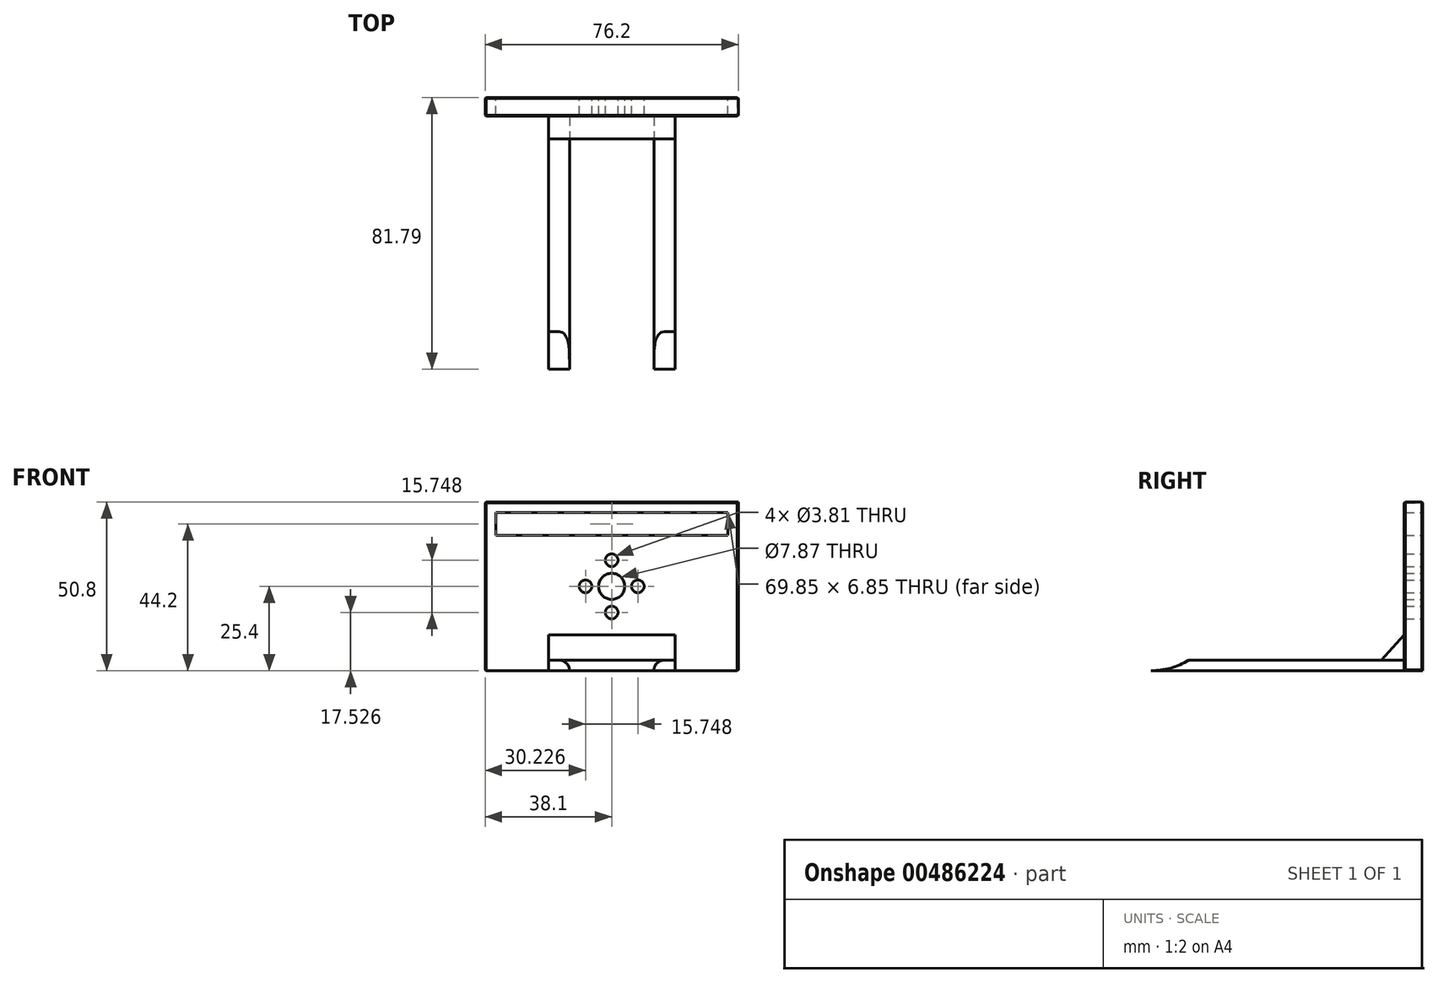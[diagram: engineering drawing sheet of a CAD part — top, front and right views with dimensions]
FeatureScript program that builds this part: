
annotation { "Feature Type Name" : "Feature", "Feature Type Description" : "" }
export const myFeature = defineFeature(function(context is Context, id is Id, definition is map)
    precondition{}
    {
        {
            var Q0;
            Q0=qCreatedBy(makeId("Front.planeOp"),FACE);
            var sketch = newSketch(context, id + "F0", { "sketchPlane" : qUnion([Q0])});
            skLineSegment(sketch, "E0.bottom", {"start": v(-38.1, 25.4) * mm, "end": v(38.1, 25.4) * mm});
            skLineSegment(sketch, "E0.top", {"start": v(-38.1, -25.4) * mm, "end": v(38.1, -25.4) * mm});
            skLineSegment(sketch, "E0.left", {"start": v(-38.1, 25.4) * mm, "end": v(-38.1, -25.4) * mm});
            skLineSegment(sketch, "E0.right", {"start": v(38.1, 25.4) * mm, "end": v(38.1, -25.4) * mm});
            skPoint(sketch, "E0.middle", {"position": v(0, 0) * mm});
            skSolve(sketch);
        }
        {
            var Q0;
            Q0 = qSketchRegion(id + "F0", true);
            extrude(context, id + "F1", {"entities" : qUnion([Q0]), "depth" : 5.6 * mm, "offsetDistance" : 25.4 * mm});
        }
        {
            var Q0;
            Q0=makeQuery(id+"F1.opExtrude","SWEPT_FACE",FACE,{"disambiguationData":[OSD([sQuery(id+"F0.wireOp",EDGE,"E0.top")])]});
            var sketch = newSketch(context, id + "F2", { "sketchPlane" : qUnion([Q0])});
            skLineSegment(sketch, "E1", {"start": v(0, 5.59) * mm, "end": v(38.1, 5.59) * mm, "construction": true});
            skLineSegment(sketch, "E2", {"start": v(38.1, 5.59) * mm, "end": v(0, 5.59) * mm, "construction": true});
            skLineSegment(sketch, "E3", {"start": v(0, 5.59) * mm, "end": v(-38.1, 5.59) * mm, "construction": true});
            skLineSegment(sketch, "E4", {"start": v(-38.1, 5.59) * mm, "end": v(0, 5.59) * mm, "construction": true});
            skLineSegment(sketch, "E5", {"start": v(0, 5.59) * mm, "end": v(-12.7, 5.59) * mm, "construction": true});
            skLineSegment(sketch, "E6", {"start": v(-12.7, 5.59) * mm, "end": v(12.7, 5.59) * mm, "construction": true});
            skLineSegment(sketch, "E7.bottom", {"start": v(-12.7, 5.59) * mm, "end": v(-19.05, 5.59) * mm});
            skLineSegment(sketch, "E7.top", {"start": v(-12.7, 81.79) * mm, "end": v(-19.05, 81.79) * mm});
            skLineSegment(sketch, "E7.left", {"start": v(-12.7, 5.59) * mm, "end": v(-12.7, 81.79) * mm});
            skLineSegment(sketch, "E7.right", {"start": v(-19.05, 5.59) * mm, "end": v(-19.05, 81.79) * mm});
            skLineSegment(sketch, "E8", {"start": v(0, 5.59) * mm, "end": v(0, 37.12) * mm, "construction": true});
            skLineSegment(sketch, "E9.MirrorCS", {"start": v(12.7, 5.59) * mm, "end": v(12.7, 81.79) * mm});
            skLineSegment(sketch, "E10.MirrorCS", {"start": v(19.05, 5.59) * mm, "end": v(19.05, 81.79) * mm});
            skLineSegment(sketch, "E11.MirrorCS", {"start": v(12.7, 81.79) * mm, "end": v(19.05, 81.79) * mm});
            skSolve(sketch);
        }
        {
            var Q0;
            Q0 = qSketchRegion(id + "F2", true);
            var Q1;
            {var subQ0=sQuery(id+"F2.wireOp",EDGE,"E9.MirrorCS");Q1=makeQuery(id+"F2.imprint","IMPRINT",FACE,{"disambiguationData":[TD([[makeQuery(id+"F2.imprint","IMPRINT",EDGE,{"derivedFrom":subQ0}),-1.0]])]});}
            extrude(context, id + "F3", {"entities" : qUnion([Q0, Q1]), "operationType" : NewBodyOperationType.ADD, "oppositeDirection" : true, "depth" : 3.17 * mm, "offsetDistance" : 25.4 * mm});
        }
        {
            var Q0;
            Q0=makeQuery(id+"F3.opExtrude","SWEPT_FACE",FACE,{"disambiguationData":[OSD([sQuery(id+"F2.wireOp",EDGE,"E7.right")])]});
            var sketch = newSketch(context, id + "F4", { "sketchPlane" : qUnion([Q0])});
            skLineSegment(sketch, "E12", {"start": v(5.59, -25.4) * mm, "end": v(5.59, -14.56) * mm});
            skLineSegment(sketch, "E13", {"start": v(5.59, -14.56) * mm, "end": v(12.47, -22.23) * mm});
            skLineSegment(sketch, "E14", {"start": v(5.59, -22.23) * mm, "end": v(12.47, -22.23) * mm});
            skSolve(sketch);
        }
        {
            var Q0;
            Q0 = qSketchRegion(id + "F4", true);
            extrude(context, id + "F5", {"entities" : qUnion([Q0]), "oppositeDirection" : true, "depth" : 38.1 * mm, "offsetDistance" : 25.4 * mm});
        }
        {
            var Q0;
            Q0=makeQuery(id+"F3.opExtrude","SWEPT_FACE",FACE,{"disambiguationData":[OSD([sQuery(id+"F2.wireOp",EDGE,"E7.right")])]});
            var sketch = newSketch(context, id + "F6", { "sketchPlane" : qUnion([Q0])});
            skLineSegment(sketch, "E15", {"start": v(53.3, -22.23) * mm, "end": v(53.3, -25.4) * mm});
            skArc(sketch, "E16", {"start": v(53.3, -22.22) * mm, "mid": v(67.24, -26.5) * mm, "end": v(81.79, -25.4) * mm});
            skLineSegment(sketch, "E17", {"start": v(53.3, -25.4) * mm, "end": v(81.79, -25.4) * mm});
            skLineSegment(sketch, "E18", {"start": v(81.79, -22.23) * mm, "end": v(53.3, -22.23) * mm});
            skSolve(sketch);
        }
        {
            var Q0;
            Q0=makeQuery(id+"F6.imprint","IMPRINT",FACE,{"disambiguationData":[TD([[makeQuery(id+"F6.imprint","IMPRINT",EDGE,{"derivedFrom":sQuery(id+"F6.wireOp",EDGE,"E16")}),1.0]])]});
            extrude(context, id + "F7", {"entities" : qUnion([Q0]), "operationType" : NewBodyOperationType.REMOVE, "oppositeDirection" : true, "depth" : 254 * mm, "offsetDistance" : 25.4 * mm});
        }
        {
            var Q0;
            Q0=makeQuery(id+"F1.opExtrude","CAP_FACE",FACE,{"disambiguationData":[OSD([sQuery(id+"F0.wireOp",EDGE,"E0.bottom"),sQuery(id+"F0.wireOp",EDGE,"E0.top"),sQuery(id+"F0.wireOp",EDGE,"E0.left"),sQuery(id+"F0.wireOp",EDGE,"E0.right")])],"isStart":true});
            var sketch = newSketch(context, id + "F8", { "sketchPlane" : qUnion([Q0])});
            skLineSegment(sketch, "E19", {"start": v(-38.1, 0) * mm, "end": v(38.1, 0) * mm, "construction": true});
            skLineSegment(sketch, "E20", {"start": v(0, 25.4) * mm, "end": v(0, -25.4) * mm, "construction": true});
            skCircle(sketch, "E21", {"center": v(0, 0) * mm, "radius": 8.58 * mm, "construction": true});
            skCircle(sketch, "E22", {"center": v(0, 0) * mm, "radius": 3.94 * mm});
            skLineSegment(sketch, "E23", {"start": v(0, 0) * mm, "end": v(0, 7.87) * mm, "construction": true});
            skCircle(sketch, "E24", {"center": v(0, 7.87) * mm, "radius": 1.9 * mm});
            skCircle(sketch, "E25.MirrorC", {"center": v(0, -7.87) * mm, "radius": 1.9 * mm});
            skLineSegment(sketch, "E26", {"start": v(0, 0) * mm, "end": v(7.87, 0) * mm, "construction": true});
            skCircle(sketch, "E27", {"center": v(7.87, 0) * mm, "radius": 1.9 * mm});
            skCircle(sketch, "E28.MirrorC", {"center": v(-7.87, 0) * mm, "radius": 1.9 * mm});
            skSolve(sketch);
        }
        {
            var Q0;
            Q0 = qSketchRegion(id + "F8", true);
            extrude(context, id + "F9", {"entities" : qUnion([Q0]), "operationType" : NewBodyOperationType.REMOVE, "oppositeDirection" : true, "depth" : 25.4 * mm, "offsetDistance" : 25.4 * mm});
        }
        {
            var Q0;
            Q0=makeQuery(id+"F1.opExtrude","CAP_FACE",FACE,{"disambiguationData":[OSD([sQuery(id+"F0.wireOp",EDGE,"E0.bottom"),sQuery(id+"F0.wireOp",EDGE,"E0.top"),sQuery(id+"F0.wireOp",EDGE,"E0.left"),sQuery(id+"F0.wireOp",EDGE,"E0.right")])],"isStart":true});
            var sketch = newSketch(context, id + "F10", { "sketchPlane" : qUnion([Q0])});
            skLineSegment(sketch, "E29", {"start": v(-38.1, 25.4) * mm, "end": v(-38.1, 22.23) * mm});
            skLineSegment(sketch, "E30", {"start": v(-38.1, 22.23) * mm, "end": v(38.1, 22.23) * mm});
            skLineSegment(sketch, "E31", {"start": v(38.1, 22.23) * mm, "end": v(38.1, 25.4) * mm});
            skLineSegment(sketch, "E32", {"start": v(38.1, 25.4) * mm, "end": v(-38.1, 25.4) * mm});
            skLineSegment(sketch, "E33", {"start": v(-38.1, 22.23) * mm, "end": v(-34.93, 22.23) * mm, "construction": true});
            skLineSegment(sketch, "E34", {"start": v(-34.93, 22.23) * mm, "end": v(-34.93, 25.4) * mm});
            skLineSegment(sketch, "E35", {"start": v(0, 0) * mm, "end": v(0, 25.4) * mm, "construction": true});
            skLineSegment(sketch, "E36.MirrorCS", {"start": v(34.92, 22.23) * mm, "end": v(34.92, 25.4) * mm});
            skLineSegment(sketch, "E37.MirrorCS", {"start": v(38.1, 25.4) * mm, "end": v(38.1, 22.23) * mm});
            skLineSegment(sketch, "E38.bottom", {"start": v(-34.93, 22.23) * mm, "end": v(34.3, 22.23) * mm});
            skLineSegment(sketch, "E38.top", {"start": v(-34.93, 15.38) * mm, "end": v(34.3, 15.38) * mm});
            skLineSegment(sketch, "E38.left", {"start": v(-34.93, 22.23) * mm, "end": v(-34.93, 15.38) * mm});
            skLineSegment(sketch, "E38.right", {"start": v(34.3, 22.23) * mm, "end": v(34.3, 15.38) * mm});
            skLineSegment(sketch, "E39.bottom", {"start": v(34.3, 15.38) * mm, "end": v(34.92, 15.38) * mm});
            skLineSegment(sketch, "E39.top", {"start": v(34.3, 22.23) * mm, "end": v(34.92, 22.23) * mm});
            skLineSegment(sketch, "E39.left", {"start": v(34.3, 15.38) * mm, "end": v(34.3, 22.23) * mm});
            skLineSegment(sketch, "E39.right", {"start": v(34.92, 15.38) * mm, "end": v(34.92, 22.23) * mm});
            skSolve(sketch);
        }
        {
            var Q0;
            Q0=makeQuery(id+"F10.imprint","IMPRINT",FACE,{"disambiguationData":[TD([[makeQuery(id+"F10.imprint","IMPRINT",EDGE,{"derivedFrom":sQuery(id+"F10.wireOp",EDGE,"E38.top")}),1.0]])]});
            var Q1;
            {var subQ2=sQuery(id+"F10.wireOp",EDGE,"E38.right");Q1=makeQuery(id+"F10.imprint","IMPRINT",FACE,{"disambiguationData":[TD([[makeQuery(id+"F10.imprint","IMPRINT",EDGE,{"derivedFrom":subQ2}),1.0]])]});}
            extrude(context, id + "F11", {"entities" : qUnion([Q0, Q1]), "operationType" : NewBodyOperationType.REMOVE, "oppositeDirection" : true, "depth" : 25.4 * mm, "offsetDistance" : 25.4 * mm});
        }
        {
            var Q0;
            Q0=makeQuery(id+"F3.opExtrude","SWEPT_FACE",FACE,{"disambiguationData":[OSD([sQuery(id+"F2.wireOp",EDGE,"E10.MirrorCS")])]});
            var sketch = newSketch(context, id + "F12", { "sketchPlane" : qUnion([Q0])});
            skLineSegment(sketch, "E40", {"start": v(-70.48, -22.23) * mm, "end": v(-70.48, -25.4) * mm});
            skArc(sketch, "E41", {"start": v(-81.79, -25.4) * mm, "mid": v(-75.92, -24.6) * mm, "end": v(-70.48, -22.23) * mm});
            skLineSegment(sketch, "E42", {"start": v(-81.79, -25.4) * mm, "end": v(-70.48, -25.4) * mm});
            skLineSegment(sketch, "E43", {"start": v(-70.48, -22.23) * mm, "end": v(-81.79, -22.23) * mm});
            skLineSegment(sketch, "E44", {"start": v(-81.79, -22.23) * mm, "end": v(-81.79, -25.4) * mm});
            skSolve(sketch);
        }
        {
            var Q0;
            Q0=makeQuery(id+"F12.imprint","IMPRINT",FACE,{"disambiguationData":[TD([[makeQuery(id+"F12.imprint","IMPRINT",EDGE,{"derivedFrom":sQuery(id+"F12.wireOp",EDGE,"E41")}),1.0]])]});
            extrude(context, id + "F13", {"entities" : qUnion([Q0]), "operationType" : NewBodyOperationType.REMOVE, "oppositeDirection" : true, "depth" : 254 * mm, "offsetDistance" : 25.4 * mm});
        }
        {
            var Q0;
            Q0=makeQuery(id+"F3.opExtrude","CAP_EDGE",EDGE,{"disambiguationData":[OSD([sQuery(id+"F2.wireOp",EDGE,"E7.left")])],"isStart":false});
            var Q1;
            Q1=makeQuery(id+"F3.opExtrude","CAP_EDGE",EDGE,{"disambiguationData":[OSD([sQuery(id+"F2.wireOp",EDGE,"E9.MirrorCS")])],"isStart":false});
            fillet(context, id + "F14", {"entities" : qUnion([Q0, Q1]), "tangentPropagation" : true, "radius" : 3.17 * mm, "defaultsChanged" : false, "vertexSettings" : [], "allowEdgeOverflow" : false});
        }
        {
            var Q0;
            Q0=makeQuery(id+"F1.opExtrude","SWEPT_EDGE",EDGE,{"disambiguationData":[OSD([sQuery(id+"F0.wireOp",EDGE,"E0.bottom"),sQuery(id+"F0.wireOp",EDGE,"E0.left")])]});
            var Q1;
            Q1=makeQuery(id+"F1.opExtrude","CAP_EDGE",EDGE,{"disambiguationData":[OSD([sQuery(id+"F0.wireOp",EDGE,"E0.bottom")])],"isStart":false});
            var Q2;
            Q2=makeQuery(id+"F1.opExtrude","CAP_EDGE",EDGE,{"disambiguationData":[OSD([sQuery(id+"F0.wireOp",EDGE,"E0.left")])],"isStart":false});
            var Q3;
            Q3=makeQuery(id+"F1.opExtrude","CAP_EDGE",EDGE,{"disambiguationData":[OSD([sQuery(id+"F0.wireOp",EDGE,"E0.right")])],"isStart":false});
            var Q4;
            Q4=makeQuery(id+"F1.opExtrude","CAP_EDGE",EDGE,{"disambiguationData":[OSD([sQuery(id+"F0.wireOp",EDGE,"E0.bottom")])],"isStart":true});
            var Q5;
            Q5=makeQuery(id+"F1.opExtrude","CAP_EDGE",EDGE,{"disambiguationData":[OSD([sQuery(id+"F0.wireOp",EDGE,"E0.right")])],"isStart":true});
            var Q6;
            Q6=makeQuery(id+"F1.opExtrude","CAP_EDGE",EDGE,{"disambiguationData":[OSD([sQuery(id+"F0.wireOp",EDGE,"E0.left")])],"isStart":true});
            var Q7;
            Q7=makeQuery(id+"F1.opExtrude","SWEPT_EDGE",EDGE,{"disambiguationData":[OSD([sQuery(id+"F0.wireOp",EDGE,"E0.top"),sQuery(id+"F0.wireOp",EDGE,"E0.left")])]});
            var Q8;
            Q8=makeQuery(id+"F1.opExtrude","SWEPT_EDGE",EDGE,{"disambiguationData":[OSD([sQuery(id+"F0.wireOp",EDGE,"E0.top"),sQuery(id+"F0.wireOp",EDGE,"E0.right")])]});
            chamfer(context, id + "F15", {"entities" : qUnion([Q0, Q1, Q2, Q3, Q4, Q5, Q6, Q7, Q8]), "width" : 0.3 * mm, "tangentPropagation" : true});
        }
    });
